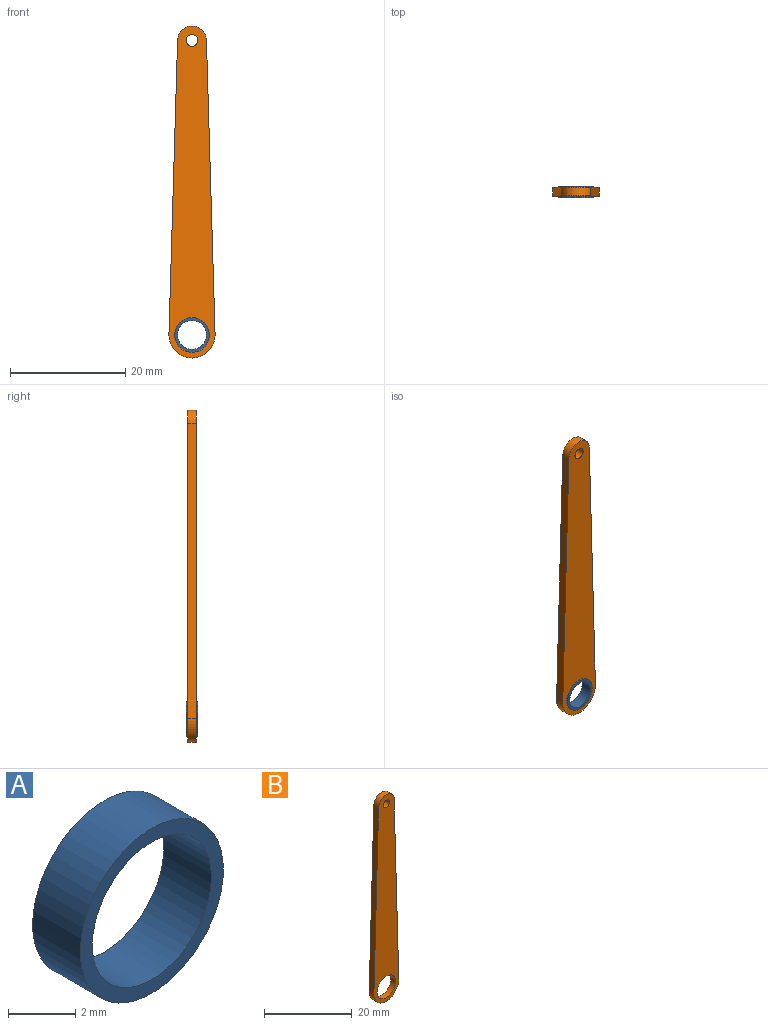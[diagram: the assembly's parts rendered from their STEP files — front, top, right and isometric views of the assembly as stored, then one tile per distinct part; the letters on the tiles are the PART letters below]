
ASSEMBLY  parts=2 mates=1
PART A: 4 faces, bbox 6x2x6 mm
  f0: cylinder r=2.5mm len=5mm, axis (0,1,0), area 31.4mm2, adj f2,f3
  f1: cylinder r=3mm len=6mm, axis (0,1,0), area 37.7mm2, adj f2,f3
  f2: plane 6x6mm, normal (0,-1,0), area 8.6mm2, adj f0,f1
  f3: plane 6x6mm, normal (0,1,0), area 8.6mm2, adj f0,f1
PART B: 8 faces, bbox 8x1.5x57.5 mm
  f0: cylinder r=2.5mm len=5mm, axis (0,1,0), area 11.6mm2, adj f1,f5,f6,f7
  f1: plane 50.96x1.5mm, normal (-1,0,0.03), area 76.5mm2, adj f0,f2,f6,f7
  f2: cylinder r=4mm len=8mm, axis (0,1,0), area 19.2mm2, adj f1,f5,f6,f7
  f3: cylinder r=3mm len=6mm, axis (0,1,0), area 28.3mm2, adj f6,f7
  f4: cylinder r=1mm len=2mm, axis (0,1,0), area 9.4mm2, adj f6,f7
  f5: plane 50.96x1.5mm, normal (1,0,0.03), area 76.5mm2, adj f0,f2,f6,f7
  f6: plane 57.5x8mm, normal (0,-1,0), area 335.2mm2, adj f0,f1,f2,f3,f4,f5
  f7: plane 57.5x8mm, normal (0,1,0), area 335.2mm2, adj f0,f1,f2,f3,f4,f5
PLACE A at identity
PLACE B at identity fixed
MATE fastened B.f3 <-> A.f0  axis (0,1,0) through (0,0,0)mm
